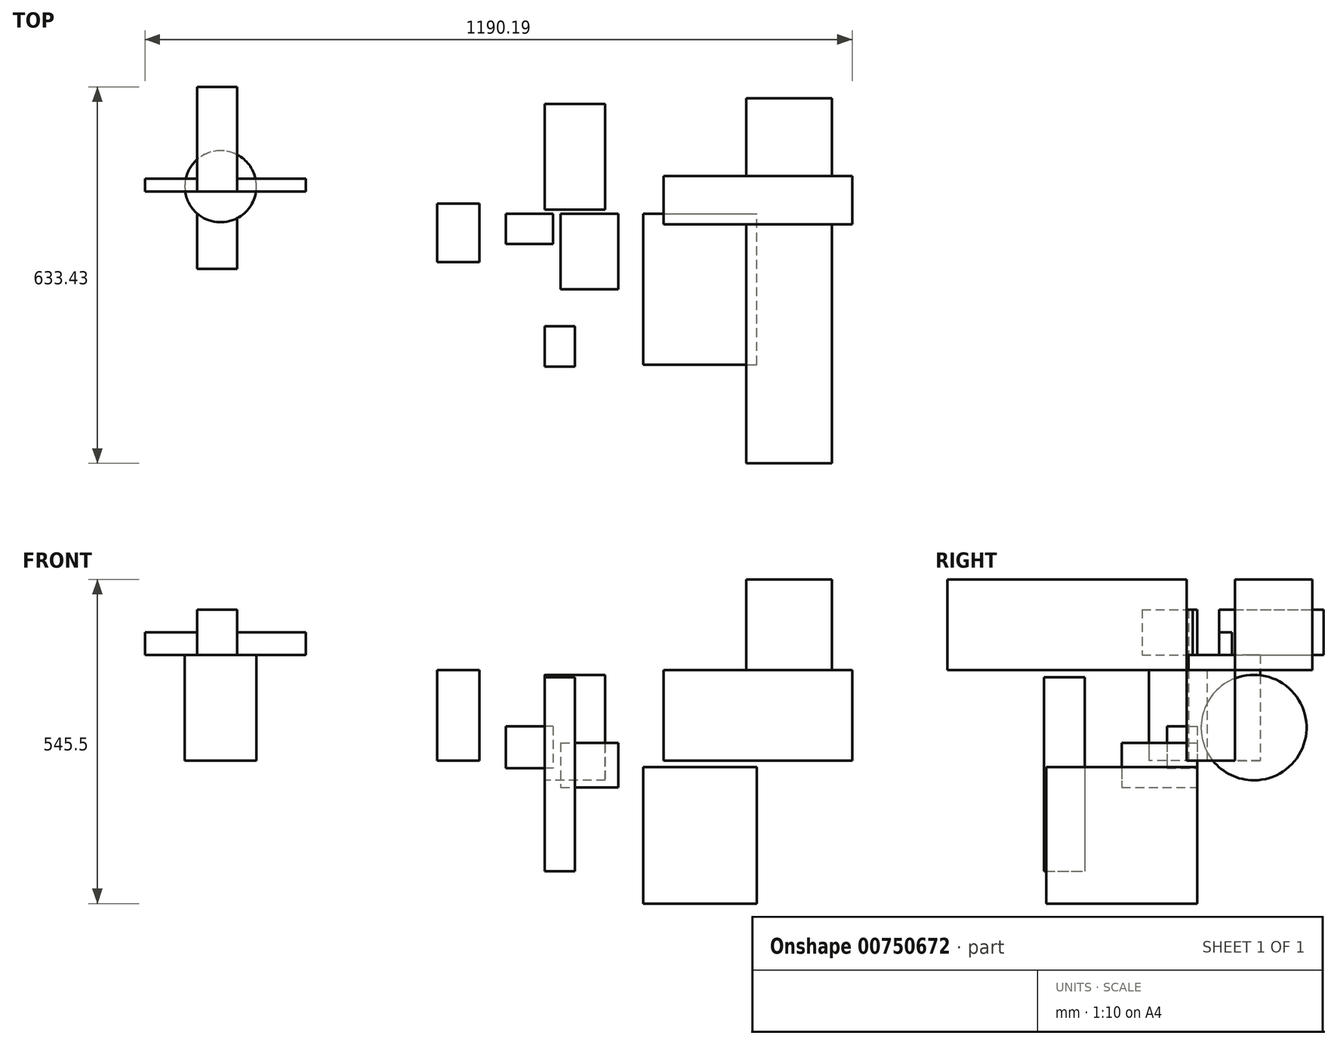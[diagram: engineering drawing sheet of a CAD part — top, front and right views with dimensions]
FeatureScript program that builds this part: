
annotation { "Feature Type Name" : "Feature", "Feature Type Description" : "" }
export const myFeature = defineFeature(function(context is Context, id is Id, definition is map)
    precondition{}
    {
        {
            var Q0;
            Q0=qCreatedBy(makeId("Front.planeOp"),FACE);
            var sketch = newSketch(context, id + "F0", { "sketchPlane" : qUnion([Q0])});
            skLineSegment(sketch, "E0.bottom", {"start": v(13.4, 57.38) * mm, "end": v(-65.52, 57.38) * mm});
            skLineSegment(sketch, "E0.top", {"start": v(13.4, -12.8) * mm, "end": v(-65.52, -12.8) * mm});
            skLineSegment(sketch, "E0.left", {"start": v(13.4, 57.38) * mm, "end": v(13.4, -12.8) * mm});
            skLineSegment(sketch, "E0.right", {"start": v(-65.52, 57.38) * mm, "end": v(-65.52, -12.8) * mm});
            skSolve(sketch);
        }
        {
            var Q0;
            Q0 = qSketchRegion(id + "F0", true);
            extrude(context, id + "F1", {"entities" : qUnion([Q0]), "depth" : 50.8 * mm, "offsetDistance" : 25.4 * mm});
        }
        {
            var Q0;
            Q0=qCreatedBy(makeId("Front.planeOp"),FACE);
            var sketch = newSketch(context, id + "F2", { "sketchPlane" : qUnion([Q0])});
            skLineSegment(sketch, "E1.bottom", {"start": v(26.67, 29.32) * mm, "end": v(123.52, 29.32) * mm});
            skLineSegment(sketch, "E1.top", {"start": v(26.67, -45.36) * mm, "end": v(123.52, -45.36) * mm});
            skLineSegment(sketch, "E1.left", {"start": v(26.67, 29.32) * mm, "end": v(26.67, -45.36) * mm});
            skLineSegment(sketch, "E1.right", {"start": v(123.52, 29.32) * mm, "end": v(123.52, -45.36) * mm});
            skSolve(sketch);
        }
        {
            var Q0;
            Q0=makeQuery(id+"F2.imprint","IMPRINT",FACE,{"disambiguationData":[TD([[makeQuery(id+"F2.imprint","IMPRINT",EDGE,{"derivedFrom":sQuery(id+"F2.wireOp",EDGE,"E1.bottom")}),-1.0]])]});
            extrude(context, id + "F3", {"entities" : qUnion([Q0]), "depth" : 127 * mm, "offsetDistance" : 25.4 * mm});
        }
        {
            var Q0;
            Q0=qCreatedBy(makeId("Top.planeOp"),FACE);
            var sketch = newSketch(context, id + "F4", { "sketchPlane" : qUnion([Q0])});
            skLineSegment(sketch, "E2.bottom", {"start": v(-181.03, 16.88) * mm, "end": v(-110.23, 16.88) * mm});
            skLineSegment(sketch, "E2.top", {"start": v(-181.03, -81.37) * mm, "end": v(-110.23, -81.37) * mm});
            skLineSegment(sketch, "E2.left", {"start": v(-181.03, 16.88) * mm, "end": v(-181.03, -81.37) * mm});
            skLineSegment(sketch, "E2.right", {"start": v(-110.23, 16.88) * mm, "end": v(-110.23, -81.37) * mm});
            skSolve(sketch);
        }
        {
            var Q0;
            Q0 = qSketchRegion(id + "F4", true);
            extrude(context, id + "F5", {"entities" : qUnion([Q0]), "depth" : 152.4 * mm, "offsetDistance" : 25.4 * mm});
        }
        {
            var Q0;
            Q0=qCreatedBy(makeId("Right.planeOp"),FACE);
            var sketch = newSketch(context, id + "F6", { "sketchPlane" : qUnion([Q0])});
            skLineSegment(sketch, "E3.bottom", {"start": v(-257.66, 140) * mm, "end": v(-189.37, 140) * mm});
            skLineSegment(sketch, "E3.top", {"start": v(-257.66, -186.13) * mm, "end": v(-189.37, -186.13) * mm});
            skLineSegment(sketch, "E3.left", {"start": v(-257.66, 140) * mm, "end": v(-257.66, -186.13) * mm});
            skLineSegment(sketch, "E3.right", {"start": v(-189.37, 140) * mm, "end": v(-189.37, -186.13) * mm});
            skSolve(sketch);
        }
        {
            var Q0;
            Q0=makeQuery(id+"F6.imprint","IMPRINT",FACE,{"disambiguationData":[TD([[makeQuery(id+"F6.imprint","IMPRINT",EDGE,{"derivedFrom":sQuery(id+"F6.wireOp",EDGE,"E3.bottom")}),-1.0]])]});
            extrude(context, id + "F7", {"entities" : qUnion([Q0]), "depth" : 50.8 * mm, "offsetDistance" : 25.4 * mm});
        }
        {
            var Q0;
            Q0=qCreatedBy(makeId("Right.planeOp"),FACE);
            var sketch = newSketch(context, id + "F8", { "sketchPlane" : qUnion([Q0])});
            skCircle(sketch, "E4", {"center": v(95.47, 55.38) * mm, "radius": 88.7 * mm});
            skSolve(sketch);
        }
        {
            var Q0;
            Q0=makeQuery(id+"F8.imprint","IMPRINT",FACE,{"disambiguationData":[TD([[makeQuery(id+"F8.imprint","IMPRINT",EDGE,{"derivedFrom":sQuery(id+"F8.wireOp",EDGE,"E4")}),1.0]])]});
            extrude(context, id + "F9", {"entities" : qUnion([Q0]), "depth" : 101.6 * mm, "offsetDistance" : 25.4 * mm});
        }
        {
            var Q0;
            Q0=qCreatedBy(makeId("Top.planeOp"),FACE);
            var sketch = newSketch(context, id + "F10", { "sketchPlane" : qUnion([Q0])});
            skLineSegment(sketch, "E5.bottom", {"start": v(199.84, 63.38) * mm, "end": v(517.15, 63.38) * mm});
            skLineSegment(sketch, "E5.top", {"start": v(199.84, -17.76) * mm, "end": v(517.15, -17.76) * mm});
            skLineSegment(sketch, "E5.left", {"start": v(199.84, 63.38) * mm, "end": v(199.84, -17.76) * mm});
            skLineSegment(sketch, "E5.right", {"start": v(517.15, 63.38) * mm, "end": v(517.15, -17.76) * mm});
            skSolve(sketch);
        }
        {
            var Q0;
            Q0=makeQuery(id+"F10.imprint","IMPRINT",FACE,{"disambiguationData":[TD([[makeQuery(id+"F10.imprint","IMPRINT",EDGE,{"derivedFrom":sQuery(id+"F10.wireOp",EDGE,"E5.bottom")}),-1.0]])]});
            extrude(context, id + "F11", {"entities" : qUnion([Q0]), "depth" : 152.4 * mm, "offsetDistance" : 25.4 * mm});
        }
        {
            var Q0;
            Q0=qCreatedBy(makeId("Front.planeOp"),FACE);
            var sketch = newSketch(context, id + "F12", { "sketchPlane" : qUnion([Q0])});
            skLineSegment(sketch, "E6.bottom", {"start": v(165.3, -10.94) * mm, "end": v(356.55, -10.94) * mm});
            skLineSegment(sketch, "E6.top", {"start": v(165.3, -240.7) * mm, "end": v(356.55, -240.7) * mm});
            skLineSegment(sketch, "E6.left", {"start": v(165.3, -10.94) * mm, "end": v(165.3, -240.7) * mm});
            skLineSegment(sketch, "E6.right", {"start": v(356.55, -10.94) * mm, "end": v(356.55, -240.7) * mm});
            skSolve(sketch);
        }
        {
            var Q0;
            Q0=makeQuery(id+"F12.imprint","IMPRINT",FACE,{"disambiguationData":[TD([[makeQuery(id+"F12.imprint","IMPRINT",EDGE,{"derivedFrom":sQuery(id+"F12.wireOp",EDGE,"E6.bottom")}),-1.0]])]});
            extrude(context, id + "F13", {"entities" : qUnion([Q0]), "depth" : 254 * mm, "offsetDistance" : 25.4 * mm});
        }
        {
            var Q0;
            Q0=qCreatedBy(makeId("Top.planeOp"),FACE);
            var sketch = newSketch(context, id + "F14", { "sketchPlane" : qUnion([Q0])});
            skCircle(sketch, "E7", {"center": v(-545.65, 45.7) * mm, "radius": 60.2 * mm});
            skSolve(sketch);
        }
        {
            var Q0;
            Q0=makeQuery(id+"F14.imprint","IMPRINT",FACE,{"disambiguationData":[TD([[makeQuery(id+"F14.imprint","IMPRINT",EDGE,{"derivedFrom":sQuery(id+"F14.wireOp",EDGE,"E7")}),1.0]])]});
            extrude(context, id + "F15", {"entities" : qUnion([Q0]), "depth" : 177.8 * mm, "offsetDistance" : 25.4 * mm});
        }
        {
            var Q0;
            Q0=makeQuery(id+"F15.opExtrude","CAP_FACE",FACE,{"disambiguationData":[OSD([sQuery(id+"F14.wireOp",EDGE,"E7")])],"isStart":false});
            var sketch = newSketch(context, id + "F16", { "sketchPlane" : qUnion([Q0])});
            skLineSegment(sketch, "E8.bottom", {"start": v(-673.04, 58.69) * mm, "end": v(-402.34, 58.69) * mm});
            skLineSegment(sketch, "E8.top", {"start": v(-673.04, 37.03) * mm, "end": v(-402.34, 37.03) * mm});
            skLineSegment(sketch, "E8.left", {"start": v(-673.04, 58.69) * mm, "end": v(-673.04, 37.03) * mm});
            skLineSegment(sketch, "E8.right", {"start": v(-402.34, 58.69) * mm, "end": v(-402.34, 37.03) * mm});
            skSolve(sketch);
        }
        {
            var Q0;
            {var subQ0=sQuery(id+"F16.wireOp",EDGE,"E8.left");Q0=makeQuery(id+"F16.imprint","IMPRINT",FACE,{"disambiguationData":[TD([[makeQuery(id+"F16.imprint","IMPRINT",EDGE,{"derivedFrom":subQ0}),1.0]])]});}
            var Q1;
            {var subQ0=sQuery(id+"F16.wireOp",EDGE,"E8.bottom");var subQ1=makeQuery(id+"F15.opExtrude","CAP_EDGE",EDGE,{"disambiguationData":[OSD([sQuery(id+"F14.wireOp",EDGE,"E7")])],"isStart":false});var subQ2=makeQuery(id+"F16.imprint","INTERSECT",VERTEX,{"disambiguationData":[OD(0.0)],"derivedFrom":[subQ1,subQ0]});Q1=makeQuery(id+"F16.imprint","IMPRINT",FACE,{"disambiguationData":[TD([[makeQuery(id+"F16.imprint","IMPRINT",EDGE,{"disambiguationData":[TD([[subQ2,-1.0]])],"derivedFrom":subQ0}),-1.0]])]});}
            var Q2;
            {var subQ0=sQuery(id+"F16.wireOp",EDGE,"E8.right");Q2=makeQuery(id+"F16.imprint","IMPRINT",FACE,{"disambiguationData":[TD([[makeQuery(id+"F16.imprint","IMPRINT",EDGE,{"derivedFrom":subQ0}),-1.0]])]});}
            extrude(context, id + "F17", {"entities" : qUnion([Q0, Q1, Q2]), "operationType" : NewBodyOperationType.ADD, "depth" : 38.1 * mm, "offsetDistance" : 25.4 * mm});
        }
        {
            var Q0;
            {var subQ0=sQuery(id+"F14.wireOp",EDGE,"E7");var subQ1=sQuery(id+"F16.wireOp",EDGE,"E8.top");Q0=makeQuery(id+"F17.boolean.opBoolean","SPLIT",FACE,{"disambiguationData":[TD([makeQuery(id+"F17.opExtrude","SWEPT_FACE",FACE,{"disambiguationData":[OSD([subQ1])]})])],"derivedFrom":makeQuery(id+"F15.opExtrude","CAP_FACE",FACE,{"disambiguationData":[OSD([subQ0])],"isStart":false})});}
            var sketch = newSketch(context, id + "F18", { "sketchPlane" : qUnion([Q0])});
            skLineSegment(sketch, "E9.bottom", {"start": v(-517.54, -92.85) * mm, "end": v(-584.92, -92.85) * mm});
            skLineSegment(sketch, "E9.top", {"start": v(-517.54, 213.1) * mm, "end": v(-584.92, 213.1) * mm});
            skLineSegment(sketch, "E9.left", {"start": v(-517.54, -92.85) * mm, "end": v(-517.54, 213.1) * mm});
            skLineSegment(sketch, "E9.right", {"start": v(-584.92, -92.85) * mm, "end": v(-584.92, 213.1) * mm});
            skSolve(sketch);
        }
        {
            var Q0;
            {var subQ0=sQuery(id+"F18.wireOp",EDGE,"E9.bottom");Q0=makeQuery(id+"F18.imprint","IMPRINT",FACE,{"disambiguationData":[TD([[makeQuery(id+"F18.imprint","IMPRINT",EDGE,{"derivedFrom":subQ0}),-1.0]])]});}
            var Q1;
            {var subQ0=sQuery(id+"F18.wireOp",EDGE,"E9.left");var subQ1=sQuery(id+"F14.wireOp",EDGE,"E7");var subQ3=makeQuery(id+"F15.opExtrude","CAP_FACE",FACE,{"disambiguationData":[OSD([subQ1])],"isStart":false});var subQ4=sQuery(id+"F16.wireOp",EDGE,"E8.top");var subQ5=makeQuery(id+"F17.opExtrude","SWEPT_FACE",FACE,{"disambiguationData":[OSD([subQ4])]});var subQ8=makeQuery(id+"F17.boolean.opBoolean","SPLIT",EDGE,{"disambiguationData":[topologyDisambiguationEdgeConnected([subQ3,subQ5])],"derivedFrom":makeQuery(id+"F17.opExtrude","CAP_EDGE",EDGE,{"disambiguationData":[OSD([subQ4])],"isStart":true})});var subQ9=makeQuery(id+"F18.imprint","INTERSECT",VERTEX,{"derivedFrom":[subQ8,subQ0]});Q1=makeQuery(id+"F18.imprint","IMPRINT",FACE,{"disambiguationData":[TD([[makeQuery(id+"F18.imprint","IMPRINT",EDGE,{"disambiguationData":[TD([[subQ9,1.0]])],"derivedFrom":subQ8}),-1.0]])]});}
            var Q2;
            {var subQ0=sQuery(id+"F18.wireOp",EDGE,"E9.top");Q2=makeQuery(id+"F18.imprint","IMPRINT",FACE,{"disambiguationData":[TD([[makeQuery(id+"F18.imprint","IMPRINT",EDGE,{"derivedFrom":subQ0}),1.0]])]});}
            extrude(context, id + "F19", {"entities" : qUnion([Q0, Q1, Q2]), "operationType" : NewBodyOperationType.ADD, "depth" : 76.2 * mm, "offsetDistance" : 25.4 * mm});
        }
        {
            var Q0;
            Q0=makeQuery(id+"F11.opExtrude","CAP_FACE",FACE,{"disambiguationData":[OSD([sQuery(id+"F10.wireOp",EDGE,"E5.bottom"),sQuery(id+"F10.wireOp",EDGE,"E5.top"),sQuery(id+"F10.wireOp",EDGE,"E5.left"),sQuery(id+"F10.wireOp",EDGE,"E5.right")])],"isStart":false});
            var sketch = newSketch(context, id + "F20", { "sketchPlane" : qUnion([Q0])});
            skLineSegment(sketch, "E10.bottom", {"start": v(338.98, 193.97) * mm, "end": v(482.72, 193.97) * mm});
            skLineSegment(sketch, "E10.top", {"start": v(338.98, -420.33) * mm, "end": v(482.72, -420.33) * mm});
            skLineSegment(sketch, "E10.left", {"start": v(338.98, 193.97) * mm, "end": v(338.98, -420.33) * mm});
            skLineSegment(sketch, "E10.right", {"start": v(482.72, 193.97) * mm, "end": v(482.72, -420.33) * mm});
            skSolve(sketch);
        }
        {
            var Q0;
            {var subQ0=sQuery(id+"F20.wireOp",EDGE,"E10.bottom");Q0=makeQuery(id+"F20.imprint","IMPRINT",FACE,{"disambiguationData":[TD([[makeQuery(id+"F20.imprint","IMPRINT",EDGE,{"derivedFrom":subQ0}),-1.0]])]});}
            var Q1;
            {var subQ0=sQuery(id+"F20.wireOp",EDGE,"E10.top");Q1=makeQuery(id+"F20.imprint","IMPRINT",FACE,{"disambiguationData":[TD([[makeQuery(id+"F20.imprint","IMPRINT",EDGE,{"derivedFrom":subQ0}),1.0]])]});}
            extrude(context, id + "F21", {"entities" : qUnion([Q0, Q1]), "depth" : 152.4 * mm, "offsetDistance" : 25.4 * mm});
        }
    });
